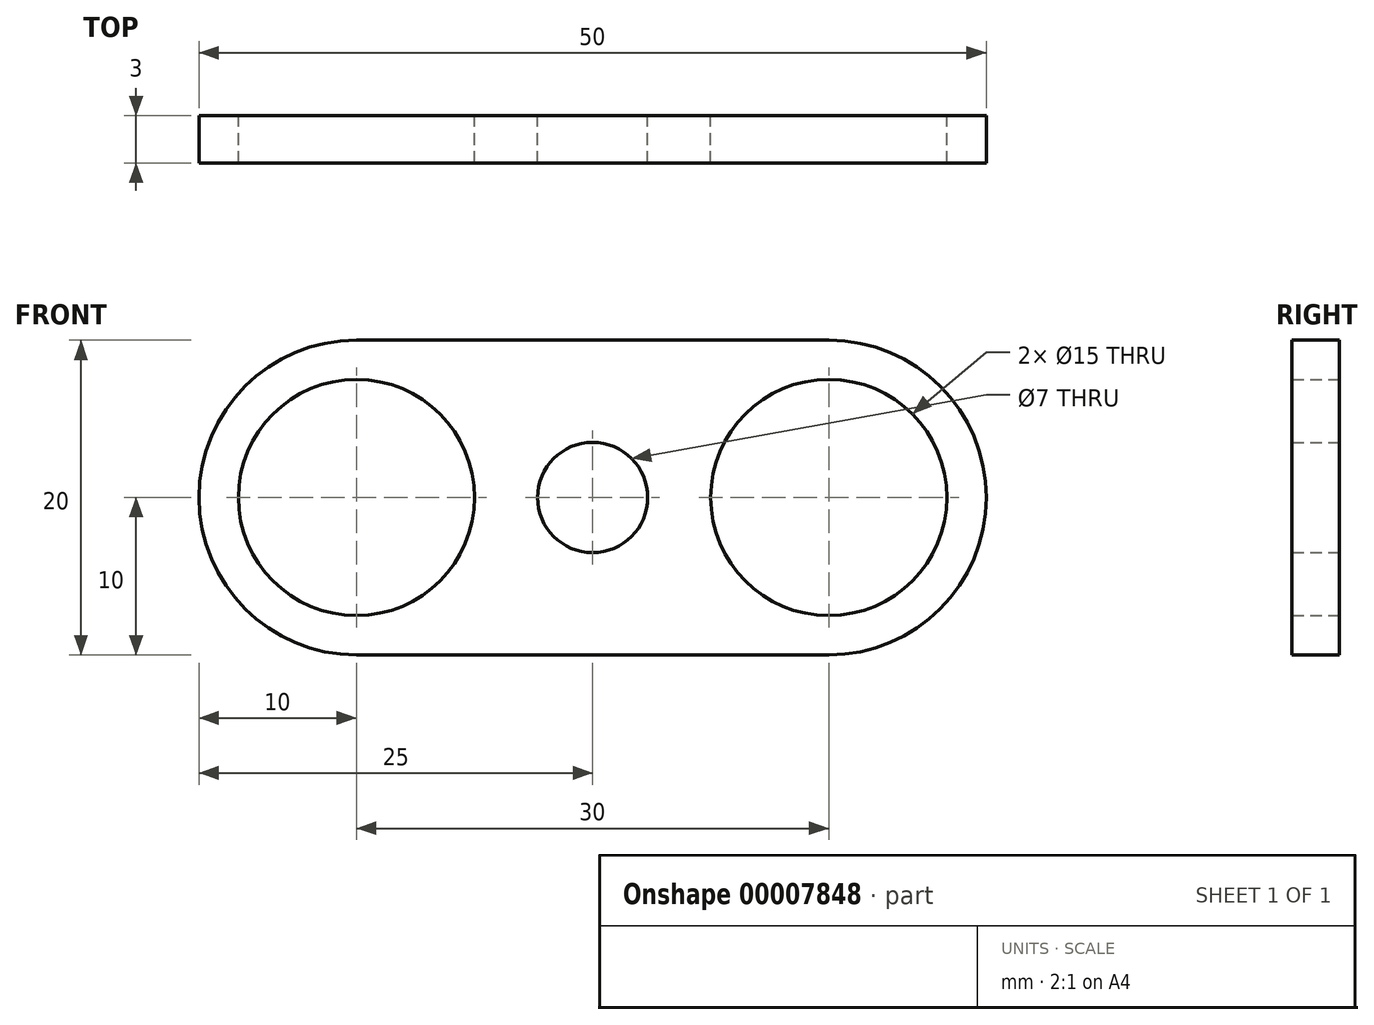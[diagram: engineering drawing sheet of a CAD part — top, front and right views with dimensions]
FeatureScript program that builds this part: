
annotation { "Feature Type Name" : "Feature", "Feature Type Description" : "" }
export const myFeature = defineFeature(function(context is Context, id is Id, definition is map)
    precondition{}
    {
        {
            var Q0;
            Q0=qCreatedBy(makeId("Front.planeOp"),FACE);
            var sketch = newSketch(context, id + "F0", { "sketchPlane" : qUnion([Q0])});
            skCircle(sketch, "E0", {"center": v(-15, 0) * mm, "radius": 7.5 * mm});
            skCircle(sketch, "E1", {"center": v(15, 0) * mm, "radius": 7.5 * mm});
            skArc(sketch, "E2", {"start": v(-15, 10) * mm, "mid": v(-25, 0) * mm, "end": v(-15, -10) * mm});
            skArc(sketch, "E3", {"start": v(15, -10) * mm, "mid": v(25, 0) * mm, "end": v(15, 10) * mm});
            skLineSegment(sketch, "E4", {"start": v(-15, 10) * mm, "end": v(15, 10) * mm});
            skLineSegment(sketch, "E5", {"start": v(-15, -10) * mm, "end": v(15, -10) * mm});
            skCircle(sketch, "E6", {"center": v(0, 0) * mm, "radius": 3.5 * mm});
            skSolve(sketch);
        }
        {
            var Q0;
            Q0=makeQuery(id+"F0.imprint","IMPRINT",FACE,{"disambiguationData":[TD([[makeQuery(id+"F0.imprint","IMPRINT",EDGE,{"derivedFrom":sQuery(id+"F0.wireOp",EDGE,"E0")}),-1.0]])]});
            extrude(context, id + "F1", {"entities" : qUnion([Q0]), "depth" : 3 * mm});
        }
    });
